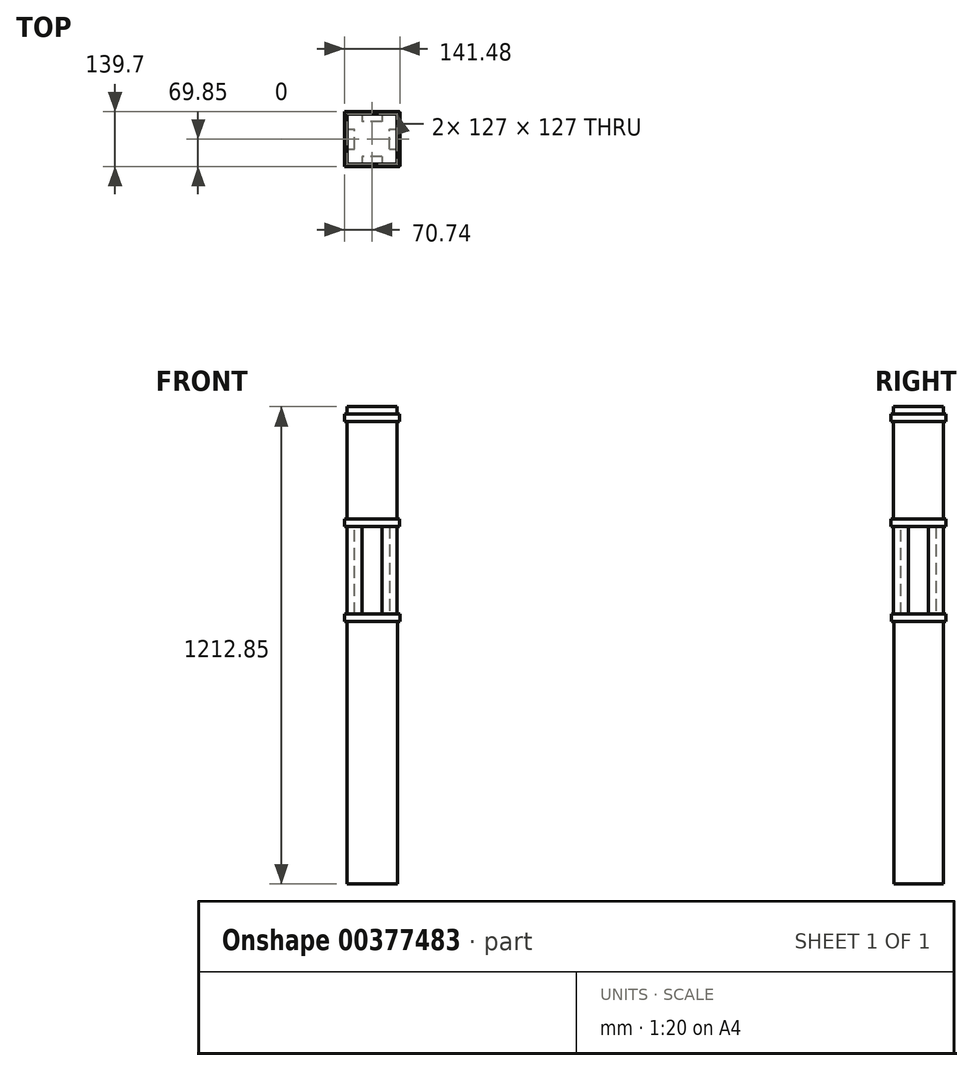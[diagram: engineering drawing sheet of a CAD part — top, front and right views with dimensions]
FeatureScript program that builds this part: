
annotation { "Feature Type Name" : "Feature", "Feature Type Description" : "" }
export const myFeature = defineFeature(function(context is Context, id is Id, definition is map)
    precondition{}
    {
        {
            var Q0;
            Q0=qCreatedBy(makeId("Top.planeOp"),FACE);
            var sketch = newSketch(context, id + "F0", { "sketchPlane" : qUnion([Q0])});
            skLineSegment(sketch, "E0.bottom", {"start": v(-64.39, 62.74) * mm, "end": v(64.39, 62.74) * mm});
            skLineSegment(sketch, "E0.top", {"start": v(-64.39, -62.74) * mm, "end": v(64.39, -62.74) * mm});
            skLineSegment(sketch, "E0.left", {"start": v(-64.39, 62.74) * mm, "end": v(-64.39, -62.74) * mm});
            skLineSegment(sketch, "E0.right", {"start": v(64.39, 62.74) * mm, "end": v(64.39, -62.74) * mm});
            skPoint(sketch, "E0.middle", {"position": v(0, 0) * mm});
            skSolve(sketch);
        }
        {
            var Q0;
            Q0=qSketchRegion(id+"F0",true);
            extrude(context, id + "F1", {"entities" : qUnion([Q0]), "depth" : 673.1 * mm, "offsetDistance" : 25.4 * mm});
        }
        {
            var Q0;
            Q0=makeQuery(id+"F1.opExtrude","CAP_FACE",FACE,{"disambiguationData":[OSD([sQuery(id+"F0.wireOp",EDGE,"E0.bottom"),sQuery(id+"F0.wireOp",EDGE,"E0.top"),sQuery(id+"F0.wireOp",EDGE,"E0.left"),sQuery(id+"F0.wireOp",EDGE,"E0.right")])],"isStart":false});
            var sketch = newSketch(context, id + "F2", { "sketchPlane" : qUnion([Q0])});
            skLineSegment(sketch, "E1.bottom", {"start": v(-44.45, 44.45) * mm, "end": v(44.45, 44.45) * mm});
            skLineSegment(sketch, "E1.top", {"start": v(-44.45, -44.45) * mm, "end": v(44.45, -44.45) * mm});
            skLineSegment(sketch, "E1.left", {"start": v(-44.45, 44.45) * mm, "end": v(-44.45, -44.45) * mm});
            skLineSegment(sketch, "E1.right", {"start": v(44.45, 44.45) * mm, "end": v(44.45, -44.45) * mm});
            skPoint(sketch, "E1.middle", {"position": v(0, 0) * mm});
            skSolve(sketch);
        }
        {
            var Q0;
            Q0=qSketchRegion(id+"F2",true);
            extrude(context, id + "F3", {"entities" : qUnion([Q0]), "operationType" : NewBodyOperationType.ADD, "depth" : 508 * mm, "offsetDistance" : 25.4 * mm});
        }
        {
            var Q0;
            Q0=makeQuery(id+"F1.opExtrude","CAP_FACE",FACE,{"disambiguationData":[OSD([sQuery(id+"F0.wireOp",EDGE,"E0.bottom"),sQuery(id+"F0.wireOp",EDGE,"E0.top"),sQuery(id+"F0.wireOp",EDGE,"E0.left"),sQuery(id+"F0.wireOp",EDGE,"E0.right")])],"isStart":false});
            var sketch = newSketch(context, id + "F4", { "sketchPlane" : qUnion([Q0])});
            skLineSegment(sketch, "E2.bottom", {"start": v(-44.45, 44.45) * mm, "end": v(44.45, 44.45) * mm});
            skLineSegment(sketch, "E2.top", {"start": v(-44.45, -44.45) * mm, "end": v(44.45, -44.45) * mm});
            skLineSegment(sketch, "E2.left", {"start": v(-44.45, 44.45) * mm, "end": v(-44.45, -44.45) * mm});
            skLineSegment(sketch, "E2.right", {"start": v(44.45, 44.45) * mm, "end": v(44.45, -44.45) * mm});
            skPoint(sketch, "E2.middle", {"position": v(0, 0) * mm});
            skLineSegment(sketch, "E3.0", {"start": v(-70.74, 69.09) * mm, "end": v(70.74, 69.09) * mm});
            skLineSegment(sketch, "E3.1", {"start": v(-70.74, 69.09) * mm, "end": v(-70.74, -69.09) * mm});
            skLineSegment(sketch, "E3.2", {"start": v(-70.74, -69.09) * mm, "end": v(70.74, -69.09) * mm});
            skLineSegment(sketch, "E3.3", {"start": v(70.74, 69.09) * mm, "end": v(70.74, -69.09) * mm});
            skSolve(sketch);
        }
        {
            var Q0;
            Q0=qSketchRegion(id+"F4",true);
            extrude(context, id + "F5", {"entities" : qUnion([Q0]), "operationType" : NewBodyOperationType.ADD, "depth" : 12.7 * mm, "offsetDistance" : 25.4 * mm});
        }
        {
            var Q0;
            Q0=makeQuery(id+"F5.opExtrude","CAP_FACE",FACE,{"disambiguationData":[OSD([sQuery(id+"F4.wireOp",EDGE,"E2.bottom"),sQuery(id+"F4.wireOp",EDGE,"E2.top"),sQuery(id+"F4.wireOp",EDGE,"E2.left"),sQuery(id+"F4.wireOp",EDGE,"E2.right"),sQuery(id+"F4.wireOp",EDGE,"E3.0"),sQuery(id+"F4.wireOp",EDGE,"E3.1"),sQuery(id+"F4.wireOp",EDGE,"E3.2"),sQuery(id+"F4.wireOp",EDGE,"E3.3")])],"isStart":true});
            var sketch = newSketch(context, id + "F6", { "sketchPlane" : qUnion([Q0])});
            skLineSegment(sketch, "E4.bottom", {"start": v(-64.39, 62.74) * mm, "end": v(64.39, 62.74) * mm});
            skLineSegment(sketch, "E4.top", {"start": v(-64.39, -62.74) * mm, "end": v(64.39, -62.74) * mm});
            skLineSegment(sketch, "E4.left", {"start": v(-64.39, 62.74) * mm, "end": v(-64.39, -62.74) * mm});
            skLineSegment(sketch, "E4.right", {"start": v(64.39, 62.74) * mm, "end": v(64.39, -62.74) * mm});
            skPoint(sketch, "E4.middle", {"position": v(0, 0) * mm});
            skLineSegment(sketch, "E5.bottom", {"start": v(-70.74, 69.09) * mm, "end": v(70.74, 69.09) * mm});
            skLineSegment(sketch, "E5.top", {"start": v(-70.74, -69.09) * mm, "end": v(70.74, -69.09) * mm});
            skLineSegment(sketch, "E5.left", {"start": v(-70.74, 69.09) * mm, "end": v(-70.74, -69.09) * mm});
            skLineSegment(sketch, "E5.right", {"start": v(70.74, 69.09) * mm, "end": v(70.74, -69.09) * mm});
            skSolve(sketch);
        }
        {
            var Q0;
            Q0=qSketchRegion(id+"F6",true);
            extrude(context, id + "F7", {"entities" : qUnion([Q0]), "operationType" : NewBodyOperationType.ADD, "depth" : 6.35 * mm, "offsetDistance" : 25.4 * mm});
        }
        {
            var Q0;
            Q0=makeQuery(id+"F5.opExtrude","CAP_FACE",FACE,{"disambiguationData":[OSD([sQuery(id+"F4.wireOp",EDGE,"E2.bottom"),sQuery(id+"F4.wireOp",EDGE,"E2.top"),sQuery(id+"F4.wireOp",EDGE,"E2.left"),sQuery(id+"F4.wireOp",EDGE,"E2.right"),sQuery(id+"F4.wireOp",EDGE,"E3.0"),sQuery(id+"F4.wireOp",EDGE,"E3.1"),sQuery(id+"F4.wireOp",EDGE,"E3.2"),sQuery(id+"F4.wireOp",EDGE,"E3.3")])],"isStart":false});
            var sketch = newSketch(context, id + "F8", { "sketchPlane" : qUnion([Q0])});
            skLineSegment(sketch, "E6.bottom", {"start": v(63.5, 63.5) * mm, "end": v(25.4, 63.5) * mm});
            skLineSegment(sketch, "E6.top", {"start": v(63.5, 25.4) * mm, "end": v(25.4, 25.4) * mm});
            skLineSegment(sketch, "E6.left", {"start": v(63.5, 63.5) * mm, "end": v(63.5, 25.4) * mm});
            skLineSegment(sketch, "E6.right", {"start": v(25.4, 63.5) * mm, "end": v(25.4, 25.4) * mm});
            skPoint(sketch, "E6.middle", {"position": v(44.45, 44.45) * mm});
            skLineSegment(sketch, "E7.bottom", {"start": v(25.4, -25.4) * mm, "end": v(63.5, -25.4) * mm});
            skLineSegment(sketch, "E7.top", {"start": v(25.4, -63.5) * mm, "end": v(63.5, -63.5) * mm});
            skLineSegment(sketch, "E7.left", {"start": v(25.4, -25.4) * mm, "end": v(25.4, -63.5) * mm});
            skLineSegment(sketch, "E7.right", {"start": v(63.5, -25.4) * mm, "end": v(63.5, -63.5) * mm});
            skPoint(sketch, "E7.middle", {"position": v(44.45, -44.45) * mm});
            skLineSegment(sketch, "E8.bottom", {"start": v(-63.5, -63.5) * mm, "end": v(-25.4, -63.5) * mm});
            skLineSegment(sketch, "E8.top", {"start": v(-63.5, -25.4) * mm, "end": v(-25.4, -25.4) * mm});
            skLineSegment(sketch, "E8.left", {"start": v(-63.5, -63.5) * mm, "end": v(-63.5, -25.4) * mm});
            skLineSegment(sketch, "E8.right", {"start": v(-25.4, -63.5) * mm, "end": v(-25.4, -25.4) * mm});
            skPoint(sketch, "E8.middle", {"position": v(-44.45, -44.45) * mm});
            skLineSegment(sketch, "E9.bottom", {"start": v(-63.5, 63.5) * mm, "end": v(-25.4, 63.5) * mm});
            skLineSegment(sketch, "E9.top", {"start": v(-63.5, 25.4) * mm, "end": v(-25.4, 25.4) * mm});
            skLineSegment(sketch, "E9.left", {"start": v(-63.5, 63.5) * mm, "end": v(-63.5, 25.4) * mm});
            skLineSegment(sketch, "E9.right", {"start": v(-25.4, 63.5) * mm, "end": v(-25.4, 25.4) * mm});
            skPoint(sketch, "E9.middle", {"position": v(-44.45, 44.45) * mm});
            skSolve(sketch);
        }
        {
            var Q0;
            Q0=qSketchRegion(id+"F8",true);
            extrude(context, id + "F9", {"entities" : qUnion([Q0]), "operationType" : NewBodyOperationType.ADD, "depth" : 495.3 * mm, "offsetDistance" : 25.4 * mm});
        }
        {
            var Q0;
            Q0=makeQuery(id+"F9.boolean.opBoolean","MERGE",FACE,{"derivedFrom":[makeQuery(id+"F3.opExtrude","CAP_FACE",FACE,{"disambiguationData":[OSD([sQuery(id+"F2.wireOp",EDGE,"E1.bottom"),sQuery(id+"F2.wireOp",EDGE,"E1.top"),sQuery(id+"F2.wireOp",EDGE,"E1.left"),sQuery(id+"F2.wireOp",EDGE,"E1.right")])],"isStart":false}),makeQuery(id+"F9.opExtrude","CAP_FACE",FACE,{"disambiguationData":[OSD([sQuery(id+"F8.wireOp",EDGE,"E6.bottom"),sQuery(id+"F8.wireOp",EDGE,"E6.top"),sQuery(id+"F8.wireOp",EDGE,"E6.left"),sQuery(id+"F8.wireOp",EDGE,"E6.right")])],"isStart":false}),makeQuery(id+"F9.opExtrude","CAP_FACE",FACE,{"disambiguationData":[OSD([sQuery(id+"F8.wireOp",EDGE,"E7.bottom"),sQuery(id+"F8.wireOp",EDGE,"E7.top"),sQuery(id+"F8.wireOp",EDGE,"E7.left"),sQuery(id+"F8.wireOp",EDGE,"E7.right")])],"isStart":false}),makeQuery(id+"F9.opExtrude","CAP_FACE",FACE,{"disambiguationData":[OSD([sQuery(id+"F8.wireOp",EDGE,"E8.bottom"),sQuery(id+"F8.wireOp",EDGE,"E8.top"),sQuery(id+"F8.wireOp",EDGE,"E8.left"),sQuery(id+"F8.wireOp",EDGE,"E8.right")])],"isStart":false}),makeQuery(id+"F9.opExtrude","CAP_FACE",FACE,{"disambiguationData":[OSD([sQuery(id+"F8.wireOp",EDGE,"E9.bottom"),sQuery(id+"F8.wireOp",EDGE,"E9.top"),sQuery(id+"F8.wireOp",EDGE,"E9.left"),sQuery(id+"F8.wireOp",EDGE,"E9.right")])],"isStart":false})]});
            var sketch = newSketch(context, id + "F10", { "sketchPlane" : qUnion([Q0])});
            skLineSegment(sketch, "E10.bottom", {"start": v(-63.5, -63.5) * mm, "end": v(63.5, -63.5) * mm});
            skLineSegment(sketch, "E10.top", {"start": v(-63.5, 63.5) * mm, "end": v(63.5, 63.5) * mm});
            skLineSegment(sketch, "E10.left", {"start": v(-63.5, -63.5) * mm, "end": v(-63.5, 63.5) * mm});
            skLineSegment(sketch, "E10.right", {"start": v(63.5, -63.5) * mm, "end": v(63.5, 63.5) * mm});
            skPoint(sketch, "E10.middle", {"position": v(0, 0) * mm});
            skLineSegment(sketch, "E11.0", {"start": v(-69.85, 69.85) * mm, "end": v(69.85, 69.85) * mm});
            skLineSegment(sketch, "E11.1", {"start": v(-69.85, -69.85) * mm, "end": v(-69.85, 69.85) * mm});
            skLineSegment(sketch, "E11.2", {"start": v(-69.85, -69.85) * mm, "end": v(69.85, -69.85) * mm});
            skLineSegment(sketch, "E11.3", {"start": v(69.85, -69.85) * mm, "end": v(69.85, 69.85) * mm});
            skSolve(sketch);
        }
        {
            var Q0;
            Q0=qSketchRegion(id+"F10",true);
            extrude(context, id + "F11", {"entities" : qUnion([Q0]), "operationType" : NewBodyOperationType.ADD, "oppositeDirection" : true, "depth" : 6.35 * mm, "offsetDistance" : 25.4 * mm});
        }
        {
            var Q0;
            Q0=makeQuery(id+"F11.boolean.opBoolean","MERGE",FACE,{"derivedFrom":[makeQuery(id+"F9.boolean.opBoolean","MERGE",FACE,{"derivedFrom":[makeQuery(id+"F3.opExtrude","CAP_FACE",FACE,{"disambiguationData":[OSD([sQuery(id+"F2.wireOp",EDGE,"E1.bottom"),sQuery(id+"F2.wireOp",EDGE,"E1.top"),sQuery(id+"F2.wireOp",EDGE,"E1.left"),sQuery(id+"F2.wireOp",EDGE,"E1.right")])],"isStart":false}),makeQuery(id+"F9.opExtrude","CAP_FACE",FACE,{"disambiguationData":[OSD([sQuery(id+"F8.wireOp",EDGE,"E6.bottom"),sQuery(id+"F8.wireOp",EDGE,"E6.top"),sQuery(id+"F8.wireOp",EDGE,"E6.left"),sQuery(id+"F8.wireOp",EDGE,"E6.right")])],"isStart":false}),makeQuery(id+"F9.opExtrude","CAP_FACE",FACE,{"disambiguationData":[OSD([sQuery(id+"F8.wireOp",EDGE,"E7.bottom"),sQuery(id+"F8.wireOp",EDGE,"E7.top"),sQuery(id+"F8.wireOp",EDGE,"E7.left"),sQuery(id+"F8.wireOp",EDGE,"E7.right")])],"isStart":false}),makeQuery(id+"F9.opExtrude","CAP_FACE",FACE,{"disambiguationData":[OSD([sQuery(id+"F8.wireOp",EDGE,"E8.bottom"),sQuery(id+"F8.wireOp",EDGE,"E8.top"),sQuery(id+"F8.wireOp",EDGE,"E8.left"),sQuery(id+"F8.wireOp",EDGE,"E8.right")])],"isStart":false}),makeQuery(id+"F9.opExtrude","CAP_FACE",FACE,{"disambiguationData":[OSD([sQuery(id+"F8.wireOp",EDGE,"E9.bottom"),sQuery(id+"F8.wireOp",EDGE,"E9.top"),sQuery(id+"F8.wireOp",EDGE,"E9.left"),sQuery(id+"F8.wireOp",EDGE,"E9.right")])],"isStart":false})]}),makeQuery(id+"F11.opExtrude","CAP_FACE",FACE,{"disambiguationData":[OSD([sQuery(id+"F10.wireOp",EDGE,"E10.bottom"),sQuery(id+"F10.wireOp",EDGE,"E10.top"),sQuery(id+"F10.wireOp",EDGE,"E10.left"),sQuery(id+"F10.wireOp",EDGE,"E10.right"),sQuery(id+"F10.wireOp",EDGE,"E11.0"),sQuery(id+"F10.wireOp",EDGE,"E11.1"),sQuery(id+"F10.wireOp",EDGE,"E11.2"),sQuery(id+"F10.wireOp",EDGE,"E11.3")])],"isStart":true})]});
            var sketch = newSketch(context, id + "F12", { "sketchPlane" : qUnion([Q0])});
            skLineSegment(sketch, "E12.bottom", {"start": v(-69.85, 69.85) * mm, "end": v(69.85, 69.85) * mm});
            skLineSegment(sketch, "E12.top", {"start": v(-69.85, -69.85) * mm, "end": v(69.85, -69.85) * mm});
            skLineSegment(sketch, "E12.left", {"start": v(-69.85, 69.85) * mm, "end": v(-69.85, -69.85) * mm});
            skLineSegment(sketch, "E12.right", {"start": v(69.85, 69.85) * mm, "end": v(69.85, -69.85) * mm});
            skPoint(sketch, "E12.middle", {"position": v(0, 0) * mm});
            skSolve(sketch);
        }
        {
            var Q0;
            Q0=qSketchRegion(id+"F12",true);
            extrude(context, id + "F13", {"entities" : qUnion([Q0]), "operationType" : NewBodyOperationType.ADD, "depth" : 12.7 * mm, "offsetDistance" : 25.4 * mm});
        }
        {
            var Q0;
            Q0=makeQuery(id+"F3.opExtrude","SWEPT_FACE",FACE,{"disambiguationData":[OSD([sQuery(id+"F2.wireOp",EDGE,"E1.right")])]});
            var sketch = newSketch(context, id + "F14", { "sketchPlane" : qUnion([Q0])});
            skLineSegment(sketch, "E13.bottom", {"start": v(-25.4, 1181.1) * mm, "end": v(25.4, 1181.1) * mm});
            skLineSegment(sketch, "E13.top", {"start": v(-25.4, 927.1) * mm, "end": v(25.4, 927.1) * mm});
            skLineSegment(sketch, "E13.left", {"start": v(-25.4, 1181.1) * mm, "end": v(-25.4, 927.1) * mm});
            skLineSegment(sketch, "E13.right", {"start": v(25.4, 1181.1) * mm, "end": v(25.4, 927.1) * mm});
            skSolve(sketch);
        }
        {
            var Q0;
            Q0 = qSketchRegion(id + "F14", true);
            extrude(context, id + "F15", {"entities" : qUnion([Q0]), "operationType" : NewBodyOperationType.ADD, "depth" : 19.05 * mm, "offsetDistance" : 25.4 * mm, "hasSecondDirection" : true, "secondDirectionOppositeDirection" : true, "secondDirectionDepth" : 107.95 * mm});
        }
        {
            var Q0;
            Q0=makeQuery(id+"F3.opExtrude","SWEPT_FACE",FACE,{"disambiguationData":[OSD([sQuery(id+"F2.wireOp",EDGE,"E1.top")])]});
            var sketch = newSketch(context, id + "F16", { "sketchPlane" : qUnion([Q0])});
            skLineSegment(sketch, "E14.bottom", {"start": v(-25.4, 1181.1) * mm, "end": v(25.4, 1181.1) * mm});
            skLineSegment(sketch, "E14.top", {"start": v(-25.4, 927.1) * mm, "end": v(25.4, 927.1) * mm});
            skLineSegment(sketch, "E14.left", {"start": v(-25.4, 1181.1) * mm, "end": v(-25.4, 927.1) * mm});
            skLineSegment(sketch, "E14.right", {"start": v(25.4, 1181.1) * mm, "end": v(25.4, 927.1) * mm});
            skSolve(sketch);
        }
        {
            var Q0;
            Q0 = qSketchRegion(id + "F16", true);
            extrude(context, id + "F17", {"entities" : qUnion([Q0]), "operationType" : NewBodyOperationType.ADD, "depth" : 19.05 * mm, "offsetDistance" : 25.4 * mm, "hasSecondDirection" : true, "secondDirectionOppositeDirection" : true, "secondDirectionDepth" : 107.95 * mm});
        }
        {
            var Q0;
            Q0=makeQuery(id+"F17.boolean.opBoolean","MERGE",FACE,{"derivedFrom":[makeQuery(id+"F9.opExtrude","SWEPT_FACE",FACE,{"disambiguationData":[OSD([sQuery(id+"F8.wireOp",EDGE,"E7.top")])]}),makeQuery(id+"F9.opExtrude","SWEPT_FACE",FACE,{"disambiguationData":[OSD([sQuery(id+"F8.wireOp",EDGE,"E8.bottom")])]}),makeQuery(id+"F17.opExtrude","CAP_FACE",FACE,{"disambiguationData":[OSD([sQuery(id+"F16.wireOp",EDGE,"E14.bottom"),sQuery(id+"F16.wireOp",EDGE,"E14.top"),sQuery(id+"F16.wireOp",EDGE,"E14.left"),sQuery(id+"F16.wireOp",EDGE,"E14.right")])],"isStart":false})]});
            var sketch = newSketch(context, id + "F18", { "sketchPlane" : qUnion([Q0])});
            skLineSegment(sketch, "E15.bottom", {"start": v(-69.85, 927.1) * mm, "end": v(69.85, 927.1) * mm});
            skLineSegment(sketch, "E15.top", {"start": v(-69.85, 908.05) * mm, "end": v(69.85, 908.05) * mm});
            skLineSegment(sketch, "E15.left", {"start": v(-69.85, 927.1) * mm, "end": v(-69.85, 908.05) * mm});
            skLineSegment(sketch, "E15.right", {"start": v(69.85, 927.1) * mm, "end": v(69.85, 908.05) * mm});
            skSolve(sketch);
        }
        {
            var Q0;
            Q0 = qSketchRegion(id + "F18", true);
            extrude(context, id + "F19", {"entities" : qUnion([Q0]), "operationType" : NewBodyOperationType.ADD, "oppositeDirection" : true, "depth" : 133.35 * mm, "offsetDistance" : 25.4 * mm, "hasSecondDirection" : true, "secondDirectionOppositeDirection" : false, "secondDirectionDepth" : 6.35 * mm});
        }
        {
            var Q0;
            Q0=makeQuery(id+"F13.opExtrude","CAP_FACE",FACE,{"disambiguationData":[OSD([sQuery(id+"F12.wireOp",EDGE,"E12.bottom"),sQuery(id+"F12.wireOp",EDGE,"E12.top"),sQuery(id+"F12.wireOp",EDGE,"E12.left"),sQuery(id+"F12.wireOp",EDGE,"E12.right")])],"isStart":false});
            var sketch = newSketch(context, id + "F20", { "sketchPlane" : qUnion([Q0])});
            skLineSegment(sketch, "E16.0", {"start": v(-63.5, 63.5) * mm, "end": v(63.5, 63.5) * mm});
            skLineSegment(sketch, "E16.1", {"start": v(-63.5, -63.5) * mm, "end": v(-63.5, 63.5) * mm});
            skLineSegment(sketch, "E16.2", {"start": v(-63.5, -63.5) * mm, "end": v(63.5, -63.5) * mm});
            skLineSegment(sketch, "E16.3", {"start": v(63.5, -63.5) * mm, "end": v(63.5, 63.5) * mm});
            skSolve(sketch);
        }
        {
            var Q0;
            Q0 = qSketchRegion(id + "F20", true);
            extrude(context, id + "F21", {"entities" : qUnion([Q0]), "operationType" : NewBodyOperationType.ADD, "depth" : 19.05 * mm, "offsetDistance" : 25.4 * mm});
        }
    });
